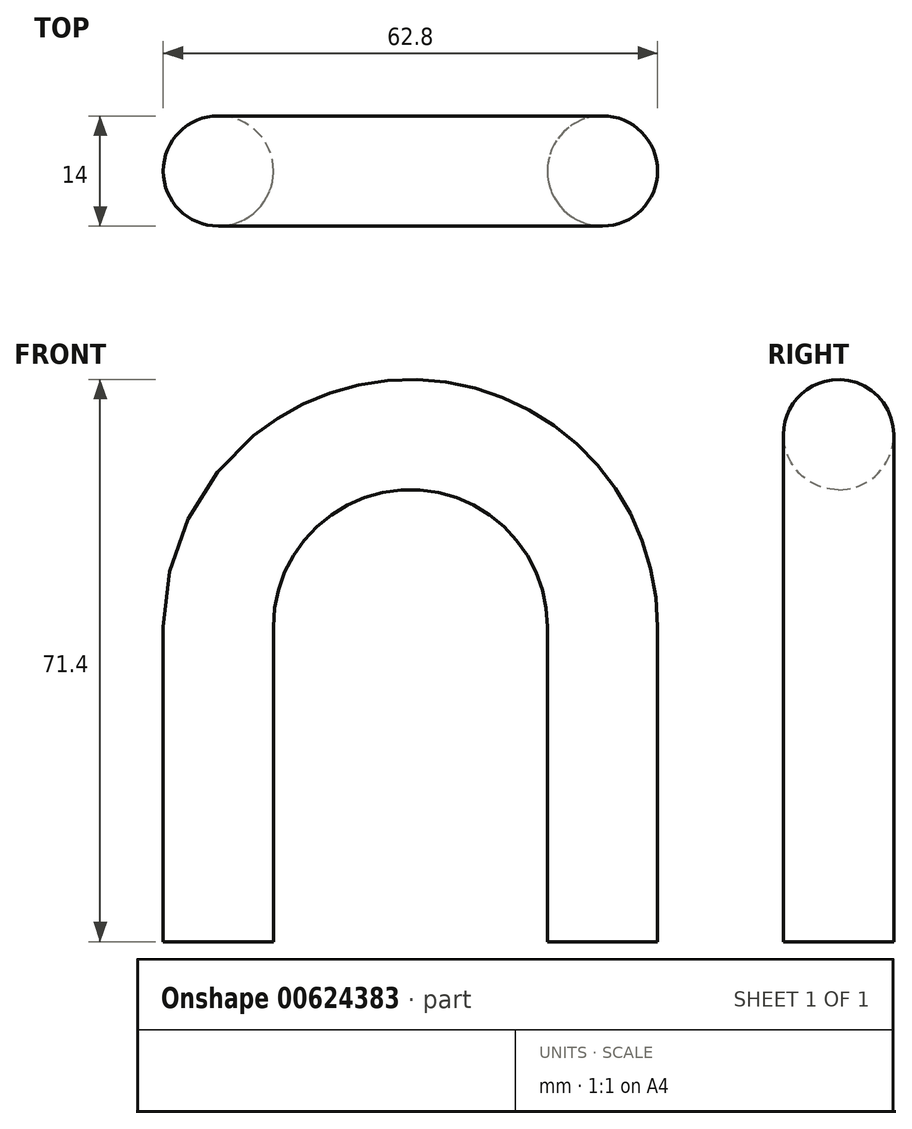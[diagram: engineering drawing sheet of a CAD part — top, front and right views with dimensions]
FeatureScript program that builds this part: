
annotation { "Feature Type Name" : "Feature", "Feature Type Description" : "" }
export const myFeature = defineFeature(function(context is Context, id is Id, definition is map)
    precondition{}
    {
        {
            var Q0;
            Q0=qCreatedBy(makeId("Top.planeOp"),FACE);
            var sketch = newSketch(context, id + "F0", { "sketchPlane" : qUnion([Q0])});
            skCircle(sketch, "E0", {"center": v(-21.03, 0) * mm, "radius": 7 * mm});
            skSolve(sketch);
        }
        {
            var Q0;
            Q0=qCreatedBy(makeId("Front.planeOp"),FACE);
            var sketch = newSketch(context, id + "F1", { "sketchPlane" : qUnion([Q0])});
            skLineSegment(sketch, "E1", {"start": v(-50.67, 0) * mm, "end": v(-50.67, 40) * mm});
            skArc(sketch, "E2", {"start": v(57.41, 40) * mm, "mid": v(3.37, 94.04) * mm, "end": v(-50.67, 40) * mm});
            skLineSegment(sketch, "E3", {"start": v(57.41, 40) * mm, "end": v(57.41, 0) * mm});
            skSolve(sketch);
        }
        {
            var Q0;
            Q0=makeQuery(id+"F0.imprint","IMPRINT",FACE,{"disambiguationData":[TD([[makeQuery(id+"F0.imprint","IMPRINT",EDGE,{"derivedFrom":sQuery(id+"F0.wireOp",EDGE,"E0")}),1.0]])]});
            var Q1;
            Q1=sQuery(id+"F1.wireOp",EDGE,"E1");
            var Q2;
            Q2=sQuery(id+"F1.wireOp",EDGE,"E2");
            var Q3;
            Q3=sQuery(id+"F1.wireOp",EDGE,"E3");
            sweep(context, id + "F2", {"profiles" : qUnion([Q0]), "path" : qUnion([Q1, Q2, Q3])});
        }
    });
